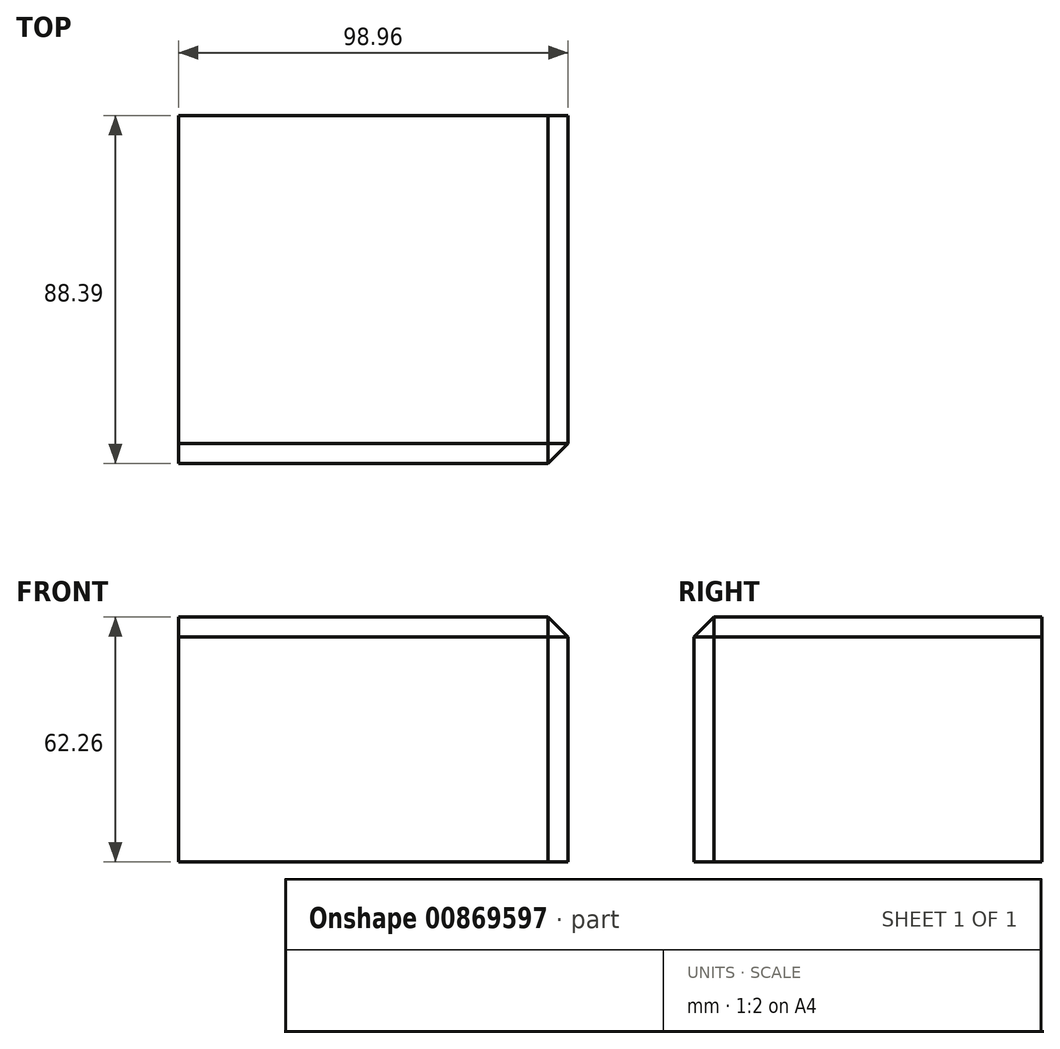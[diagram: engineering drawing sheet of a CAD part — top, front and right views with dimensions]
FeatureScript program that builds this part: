
annotation { "Feature Type Name" : "Feature", "Feature Type Description" : "" }
export const myFeature = defineFeature(function(context is Context, id is Id, definition is map)
    precondition{}
    {
        {
            var Q0;
            Q0=qCreatedBy(makeId("Front.planeOp"),FACE);
            var sketch = newSketch(context, id + "F0", { "sketchPlane" : qUnion([Q0])});
            skLineSegment(sketch, "E0.bottom", {"start": v(49.48, -31.13) * mm, "end": v(-49.48, -31.13) * mm});
            skLineSegment(sketch, "E0.top", {"start": v(49.48, 31.13) * mm, "end": v(-49.48, 31.13) * mm});
            skLineSegment(sketch, "E0.left", {"start": v(49.48, -31.13) * mm, "end": v(49.48, 31.13) * mm});
            skLineSegment(sketch, "E0.right", {"start": v(-49.48, -31.13) * mm, "end": v(-49.48, 31.13) * mm});
            skPoint(sketch, "E0.middle", {"position": v(0, 0) * mm});
            skSolve(sketch);
        }
        {
            var Q0;
            Q0 = qSketchRegion(id + "F0", true);
            extrude(context, id + "F1", {"entities" : qUnion([Q0]), "depth" : 88.4 * mm, "offsetDistance" : 25.4 * mm});
        }
        {
            var Q0;
            Q0=makeQuery(id+"F1.opExtrude","CAP_EDGE",EDGE,{"disambiguationData":[OSD([sQuery(id+"F0.wireOp",EDGE,"E0.top")])],"isStart":false});
            var Q1;
            Q1=makeQuery(id+"F1.opExtrude","SWEPT_EDGE",EDGE,{"disambiguationData":[OSD([sQuery(id+"F0.wireOp",EDGE,"E0.top"),sQuery(id+"F0.wireOp",EDGE,"E0.left")])]});
            var Q2;
            Q2=makeQuery(id+"F1.opExtrude","CAP_EDGE",EDGE,{"disambiguationData":[OSD([sQuery(id+"F0.wireOp",EDGE,"E0.left")])],"isStart":false});
            chamfer(context, id + "F2", {"entities" : qUnion([Q0, Q1, Q2]), "width" : 5.08 * mm, "tangentPropagation" : true});
        }
    });
